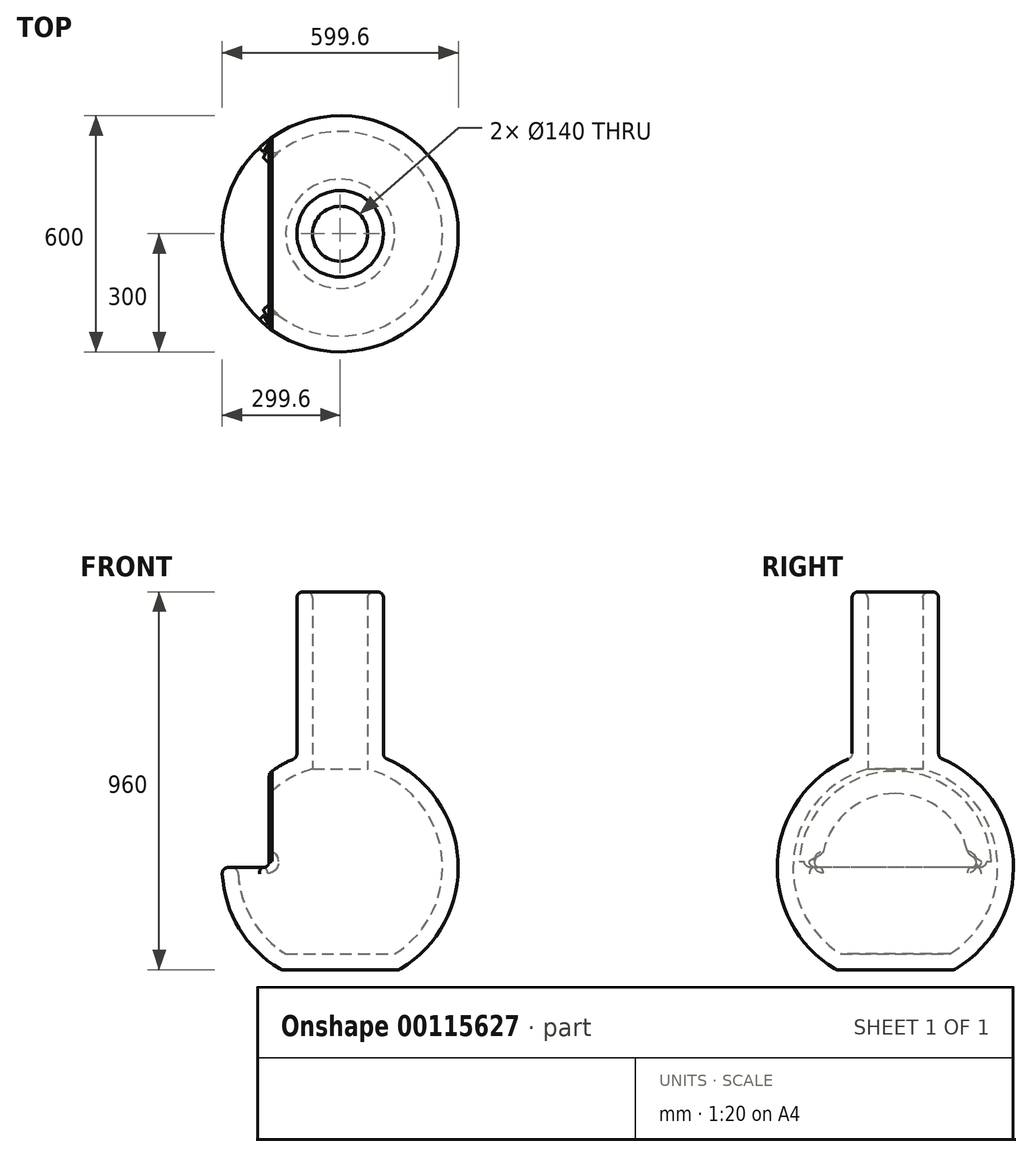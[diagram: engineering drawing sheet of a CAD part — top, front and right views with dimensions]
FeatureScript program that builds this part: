
annotation { "Feature Type Name" : "Feature", "Feature Type Description" : "" }
export const myFeature = defineFeature(function(context is Context, id is Id, definition is map)
    precondition{}
    {
        {
            var Q0;
            Q0=qCreatedBy(makeId("Front.planeOp"),FACE);
            var sketch = newSketch(context, id + "F0", { "sketchPlane" : qUnion([Q0])});
            skArc(sketch, "E0", {"start": v(0, 300) * mm, "mid": v(-254.47, 158.89) * mm, "end": v(-269.55, -131.7) * mm});
            skLineSegment(sketch, "E1", {"start": v(0, -260) * mm, "end": v(0, 700) * mm});
            skLineSegment(sketch, "E2", {"start": v(0, 700) * mm, "end": v(-110, 700) * mm});
            skLineSegment(sketch, "E3", {"start": v(-110, 700) * mm, "end": v(-110, 279.1) * mm});
            skLineSegment(sketch, "E4", {"start": v(0, 0) * mm, "end": v(-300, 0) * mm});
            skLineSegment(sketch, "E5", {"start": v(0, -260) * mm, "end": v(-149.67, -260) * mm});
            skLineSegment(sketch, "E6.MirrorCS", {"start": v(0, 260) * mm, "end": v(-149.67, 260) * mm});
            skLineSegment(sketch, "E7", {"start": v(0, -131.7) * mm, "end": v(-269.55, -131.7) * mm});
            skLineSegment(sketch, "E8", {"start": v(-180, 240) * mm, "end": v(-180, 0) * mm});
            skLineSegment(sketch, "E9", {"start": v(-180, 240) * mm, "end": v(0, 240) * mm});
            skArc(sketch, "E10", {"start": v(-269.55, -131.7) * mm, "mid": v(-219.2, -204.82) * mm, "end": v(-149.67, -260) * mm});
            skLineSegment(sketch, "E11", {"start": v(-269.55, -131.7) * mm, "end": v(-269.55, -131.7) * mm});
            skLineSegment(sketch, "E12", {"start": v(0, 131.7) * mm, "end": v(-269.55, 131.7) * mm});
            skSolve(sketch);
        }
        {
            var Q0;
            {var subQ0=sQuery(id+"F0.wireOp",EDGE,"E4");var subQ1=sQuery(id+"F0.wireOp",EDGE,"E0");var subQ2=makeQuery(id+"F0.imprint","INTERSECT",VERTEX,{"derivedFrom":[subQ1,subQ0]});Q0=makeQuery(id+"F0.imprint","IMPRINT",FACE,{"disambiguationData":[TD([[makeQuery(id+"F0.imprint","IMPRINT",EDGE,{"disambiguationData":[TD([[subQ2,1.0]])],"derivedFrom":subQ0}),-1.0]])]});}
            var Q1;
            {var subQ6=sQuery(id+"F0.wireOp",EDGE,"E7");Q1=makeQuery(id+"F0.imprint","IMPRINT",FACE,{"disambiguationData":[TD([[makeQuery(id+"F0.imprint","IMPRINT",EDGE,{"derivedFrom":subQ6}),-1.0]])]});}
            var Q2;
            {var subQ0=sQuery(id+"F0.wireOp",EDGE,"E5");Q2=makeQuery(id+"F0.imprint","IMPRINT",FACE,{"disambiguationData":[TD([[makeQuery(id+"F0.imprint","IMPRINT",EDGE,{"derivedFrom":subQ0}),-1.0]])]});}
            var Q3;
            {var subQ0=sQuery(id+"F0.wireOp",EDGE,"E6.MirrorCS");Q3=makeQuery(id+"F0.imprint","IMPRINT",FACE,{"disambiguationData":[TD([[makeQuery(id+"F0.imprint","IMPRINT",EDGE,{"derivedFrom":subQ0}),1.0]])]});}
            var Q4;
            {var subQ4=sQuery(id+"F0.wireOp",EDGE,"E6.MirrorCS");Q4=makeQuery(id+"F0.imprint","IMPRINT",FACE,{"disambiguationData":[TD([[makeQuery(id+"F0.imprint","IMPRINT",EDGE,{"derivedFrom":subQ4}),-1.0]])]});}
            var Q5;
            {var subQ4=sQuery(id+"F0.wireOp",EDGE,"E2");Q5=makeQuery(id+"F0.imprint","IMPRINT",FACE,{"disambiguationData":[TD([[makeQuery(id+"F0.imprint","IMPRINT",EDGE,{"derivedFrom":subQ4}),1.0]])]});}
            var Q6;
            {var subQ0=sQuery(id+"F0.wireOp",EDGE,"E9");Q6=makeQuery(id+"F0.imprint","IMPRINT",FACE,{"disambiguationData":[TD([[makeQuery(id+"F0.imprint","IMPRINT",EDGE,{"derivedFrom":subQ0}),-1.0]])]});}
            var Q7;
            {var subQ1=sQuery(id+"F0.wireOp",EDGE,"E0");var subQ3=sQuery(id+"F0.wireOp",EDGE,"E12");var subQ4=makeQuery(id+"F0.imprint","INTERSECT",VERTEX,{"derivedFrom":[subQ1,subQ3]});Q7=makeQuery(id+"F0.imprint","IMPRINT",FACE,{"disambiguationData":[TD([[makeQuery(id+"F0.imprint","IMPRINT",EDGE,{"disambiguationData":[TD([[subQ4,1.0]])],"derivedFrom":subQ3}),-1.0]])]});}
            var Q8;
            {var subQ0=sQuery(id+"F0.wireOp",EDGE,"E4");var subQ1=sQuery(id+"F0.wireOp",EDGE,"E1");var subQ2=makeQuery(id+"F0.imprint","INTERSECT",VERTEX,{"derivedFrom":[subQ1,subQ0]});Q8=makeQuery(id+"F0.imprint","IMPRINT",FACE,{"disambiguationData":[TD([[makeQuery(id+"F0.imprint","IMPRINT",EDGE,{"disambiguationData":[TD([[subQ2,-1.0]])],"derivedFrom":subQ1}),1.0]])]});}
            var Q9;
            Q9=sQuery(id+"F0.wireOp",EDGE,"E1");
            revolve(context, id + "F1", {"entities" : qUnion([Q0, Q1, Q2, Q3, Q4, Q5, Q6, Q7, Q8]), "axis" : qUnion([Q9]), "revolveType" : RevolveType.FULL});
        }
        {
            var Q0;
            Q0=makeQuery(id+"F1.opRevolve","CAP_FACE",FACE,{"disambiguationData":[OSD([sQuery(id+"F0.wireOp",EDGE,"E0"),sQuery(id+"F0.wireOp",EDGE,"E1"),sQuery(id+"F0.wireOp",EDGE,"E2"),sQuery(id+"F0.wireOp",EDGE,"E3"),sQuery(id+"F0.wireOp",EDGE,"E5"),sQuery(id+"F0.wireOp",EDGE,"E10")])],"isStart":false});
            var Q1;
            Q1=makeQuery(id+"F1.opRevolve","CAP_FACE",FACE,{"disambiguationData":[OSD([sQuery(id+"F0.wireOp",EDGE,"E0"),sQuery(id+"F0.wireOp",EDGE,"E1"),sQuery(id+"F0.wireOp",EDGE,"E2"),sQuery(id+"F0.wireOp",EDGE,"E3"),sQuery(id+"F0.wireOp",EDGE,"E5"),sQuery(id+"F0.wireOp",EDGE,"E10")])],"isStart":true});
            var Q2;
            Q2=makeQuery(id+"F1.opRevolve","SWEPT_FACE",FACE,{"disambiguationData":[OSD([sQuery(id+"F0.wireOp",EDGE,"E2")])]});
            shell(context, id + "F2", {"entities" : qUnion([Q0, Q1, Q2]), "thickness" : 40 * mm});
        }
        {
            var Q0;
            {var subQ0=sQuery(id+"F0.wireOp",EDGE,"E4");var subQ1=sQuery(id+"F0.wireOp",EDGE,"E0");var subQ2=makeQuery(id+"F0.imprint","INTERSECT",VERTEX,{"derivedFrom":[subQ1,subQ0]});Q0=makeQuery(id+"F0.imprint","IMPRINT",FACE,{"disambiguationData":[TD([[makeQuery(id+"F0.imprint","IMPRINT",EDGE,{"disambiguationData":[TD([[subQ2,1.0]])],"derivedFrom":subQ1}),1.0]])]});}
            var Q1;
            {var subQ1=sQuery(id+"F0.wireOp",EDGE,"E0");var subQ3=sQuery(id+"F0.wireOp",EDGE,"E12");var subQ4=makeQuery(id+"F0.imprint","INTERSECT",VERTEX,{"derivedFrom":[subQ1,subQ3]});Q1=makeQuery(id+"F0.imprint","IMPRINT",FACE,{"disambiguationData":[TD([[makeQuery(id+"F0.imprint","IMPRINT",EDGE,{"disambiguationData":[TD([[subQ4,1.0]])],"derivedFrom":subQ3}),-1.0]])]});}
            extrude(context, id + "F3", {"entities" : qUnion([Q0, Q1]), "operationType" : NewBodyOperationType.REMOVE, "endBound" : BoundingType.THROUGH_ALL, "oppositeDirection" : true, "depth" : 25 * mm, "hasSecondDirection" : true, "secondDirectionOppositeDirection" : false, "secondDirectionDepth" : 239.89 * mm});
        }
        {
            var Q0;
            Q0=makeQuery(id+"F3.boolean.opBoolean","COPY",FACE,{"derivedFrom":makeQuery(id+"F3.opExtrude","SWEPT_FACE",FACE,{"disambiguationData":[OSD([sQuery(id+"F0.wireOp",EDGE,"E4")])]})});
            var Q1;
            Q1=makeQuery(id+"F1.opRevolve","SWEPT_FACE",FACE,{"disambiguationData":[OSD([sQuery(id+"F0.wireOp",EDGE,"E0"),sQuery(id+"F0.wireOp",EDGE,"E10")])]});
            fillet(context, id + "F4", {"entities" : qUnion([Q0, Q1]), "radius" : 15 * mm, "tangentPropagation" : true, "allowEdgeOverflow" : false});
        }
        {
            var Q0;
            Q0=makeQuery(id+"F1.opRevolve","SWEPT_FACE",FACE,{"disambiguationData":[OSD([sQuery(id+"F0.wireOp",EDGE,"E2")])]});
            fillet(context, id + "F5", {"entities" : qUnion([Q0]), "radius" : 15 * mm, "tangentPropagation" : true, "allowEdgeOverflow" : false});
        }
        {
            var Q0;
            Q0=makeQuery(id+"F1.opRevolve","SWEPT_BODY",BODY,{"disambiguationData":[OSD([sQuery(id+"F0.wireOp",EDGE,"E0"),sQuery(id+"F0.wireOp",EDGE,"E1"),sQuery(id+"F0.wireOp",EDGE,"E2"),sQuery(id+"F0.wireOp",EDGE,"E3"),sQuery(id+"F0.wireOp",EDGE,"E5"),sQuery(id+"F0.wireOp",EDGE,"E10")])]});
            transform(context, id + "F6", {"entities" : qUnion([Q0]), "transformType" : TransformType.TRANSLATION_3D, "dx" : 0 * mm, "dy" : 0 * mm, "dz" : 0 * mm, "makeCopy" : true});
        }
    });
